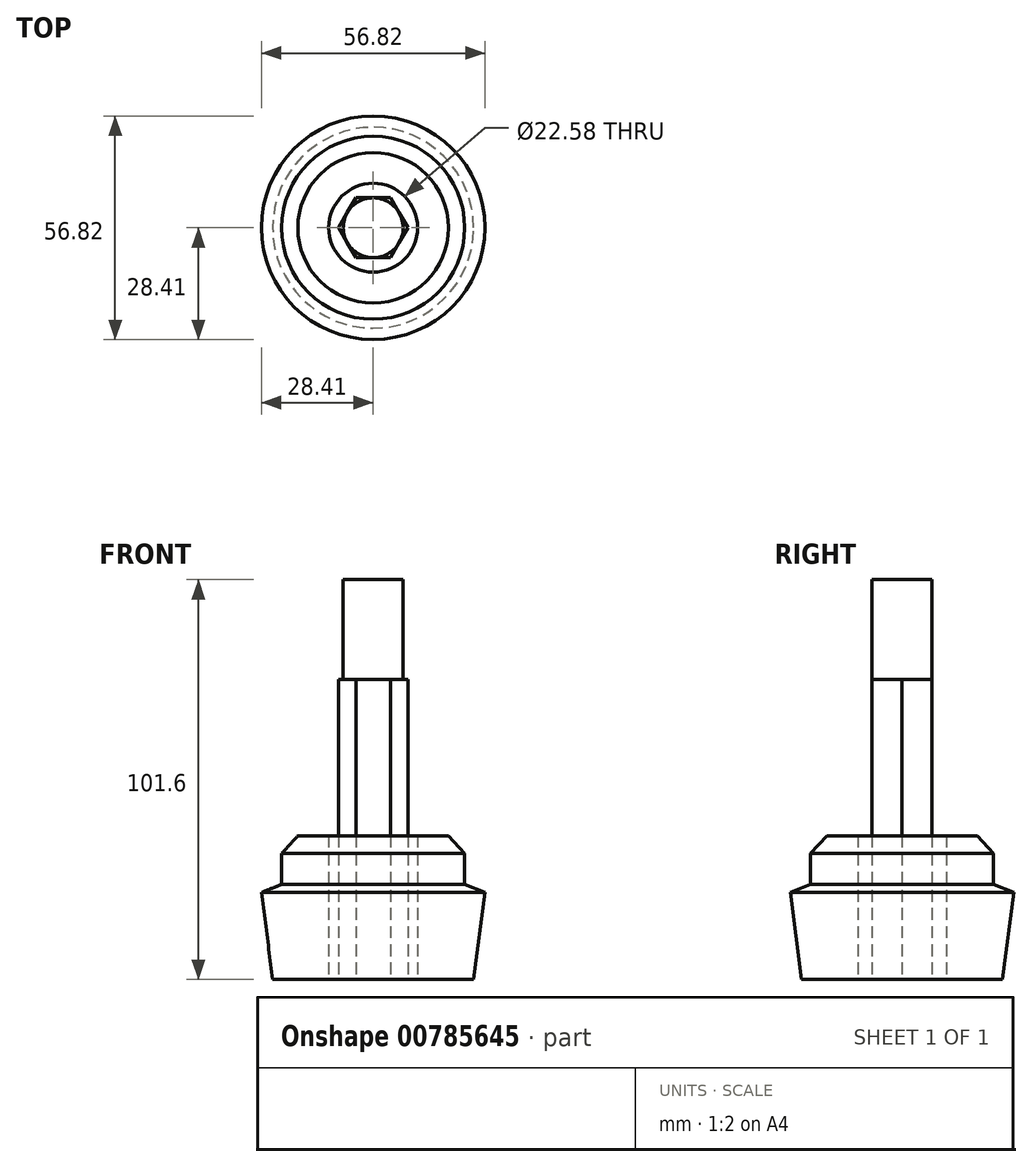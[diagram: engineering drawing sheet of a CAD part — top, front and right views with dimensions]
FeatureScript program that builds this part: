
annotation { "Feature Type Name" : "Feature", "Feature Type Description" : "" }
export const myFeature = defineFeature(function(context is Context, id is Id, definition is map)
    precondition{}
    {
        {
            var Q0;
            Q0=qCreatedBy(makeId("Front.planeOp"),FACE);
            var sketch = newSketch(context, id + "F0", { "sketchPlane" : qUnion([Q0])});
            skLineSegment(sketch, "E0", {"start": v(0, 0) * mm, "end": v(0, 43.15) * mm, "construction": true});
            skLineSegment(sketch, "E1", {"start": v(11.3, 0) * mm, "end": v(11.3, 36.55) * mm});
            skLineSegment(sketch, "E2", {"start": v(11.3, 36.55) * mm, "end": v(19.13, 36.55) * mm});
            skLineSegment(sketch, "E3", {"start": v(19.13, 36.55) * mm, "end": v(23.25, 32.01) * mm});
            skLineSegment(sketch, "E4", {"start": v(23.25, 32.01) * mm, "end": v(23.25, 24.18) * mm});
            skLineSegment(sketch, "E5", {"start": v(23.25, 24.18) * mm, "end": v(28.4, 22.12) * mm});
            skLineSegment(sketch, "E6", {"start": v(28.4, 22.12) * mm, "end": v(25.52, 0) * mm});
            skLineSegment(sketch, "E7", {"start": v(25.52, 0) * mm, "end": v(11.3, 0) * mm});
            skSolve(sketch);
        }
        {
            var Q0;
            Q0=makeQuery(id+"F0.imprint","IMPRINT",FACE,{"disambiguationData":[TD([[makeQuery(id+"F0.imprint","IMPRINT",EDGE,{"derivedFrom":sQuery(id+"F0.wireOp",EDGE,"E1")}),-1.0]])]});
            var Q1;
            Q1=sQuery(id+"F0.wireOp",EDGE,"E0");
            revolve(context, id + "F1", {"surfaceOperationType" : NewSurfaceOperationType.NEW, "entities" : qUnion([Q0]), "axis" : qUnion([Q1]), "revolveType" : RevolveType.FULL});
        }
        {
            var Q0;
            Q0=qCreatedBy(makeId("Top.planeOp"),FACE);
            var sketch = newSketch(context, id + "F2", { "sketchPlane" : qUnion([Q0])});
            skCircle(sketch, "E8.cCircle", {"center": v(0, 0) * mm, "radius": 7.6 * mm});
            skLineSegment(sketch, "E8.0", {"start": v(-4.4, 7.6) * mm, "end": v(4.4, 7.6) * mm});
            skLineSegment(sketch, "E8.1", {"start": v(4.4, 7.6) * mm, "end": v(8.79, 0) * mm});
            skLineSegment(sketch, "E8.2", {"start": v(8.79, 0) * mm, "end": v(4.4, -7.6) * mm});
            skLineSegment(sketch, "E8.3", {"start": v(4.4, -7.6) * mm, "end": v(-4.4, -7.6) * mm});
            skLineSegment(sketch, "E8.4", {"start": v(-4.4, -7.6) * mm, "end": v(-8.79, 0) * mm});
            skLineSegment(sketch, "E8.5", {"start": v(-8.79, 0) * mm, "end": v(-4.4, 7.6) * mm});
            skPoint(sketch, "E8.0.midPoint", {"position": v(0, 7.6) * mm});
            skSolve(sketch);
        }
        {
            var Q0;
            {var subQ0=sQuery(id+"F2.wireOp",EDGE,"E8.cCircle");var subQ4=makeQuery(id+"F2.imprint","INTERSECT",VERTEX,{"derivedFrom":[subQ0,sQuery(id+"F2.wireOp",EDGE,"E8.0")]});Q0=makeQuery(id+"F2.imprint","IMPRINT",FACE,{"disambiguationData":[TD([[makeQuery(id+"F2.imprint","IMPRINT",EDGE,{"disambiguationData":[TD([[subQ4,1.0]])],"derivedFrom":subQ0}),1.0]])]});}
            extrude(context, id + "F3", {"entities" : qUnion([Q0]), "depth" : 101.6 * mm, "offsetDistance" : 25.4 * mm});
        }
        {
            var Q0;
            {var subQ0=sQuery(id+"F2.wireOp",EDGE,"E8.cCircle");var subQ4=makeQuery(id+"F2.imprint","INTERSECT",VERTEX,{"derivedFrom":[subQ0,sQuery(id+"F2.wireOp",EDGE,"E8.0")]});Q0=makeQuery(id+"F2.imprint","IMPRINT",FACE,{"disambiguationData":[TD([[makeQuery(id+"F2.imprint","IMPRINT",EDGE,{"disambiguationData":[TD([[subQ4,1.0]])],"derivedFrom":subQ0}),1.0]])]});}
            var Q1;
            {var subQ0=sQuery(id+"F2.wireOp",EDGE,"E8.0");var subQ1=sQuery(id+"F2.wireOp",EDGE,"E8.cCircle");var subQ2=makeQuery(id+"F2.imprint","INTERSECT",VERTEX,{"derivedFrom":[subQ1,subQ0]});Q1=makeQuery(id+"F2.imprint","IMPRINT",FACE,{"disambiguationData":[TD([[makeQuery(id+"F2.imprint","IMPRINT",EDGE,{"disambiguationData":[TD([[subQ2,-1.0]])],"derivedFrom":subQ1}),-1.0]])]});}
            var Q2;
            {var subQ0=sQuery(id+"F2.wireOp",EDGE,"E8.0");var subQ1=sQuery(id+"F2.wireOp",EDGE,"E8.cCircle");var subQ2=makeQuery(id+"F2.imprint","INTERSECT",VERTEX,{"derivedFrom":[subQ1,subQ0]});Q2=makeQuery(id+"F2.imprint","IMPRINT",FACE,{"disambiguationData":[TD([[makeQuery(id+"F2.imprint","IMPRINT",EDGE,{"disambiguationData":[TD([[subQ2,1.0]])],"derivedFrom":subQ1}),-1.0]])]});}
            var Q3;
            {var subQ0=sQuery(id+"F2.wireOp",EDGE,"E8.1");var subQ1=sQuery(id+"F2.wireOp",EDGE,"E8.cCircle");var subQ2=makeQuery(id+"F2.imprint","INTERSECT",VERTEX,{"derivedFrom":[subQ1,subQ0]});Q3=makeQuery(id+"F2.imprint","IMPRINT",FACE,{"disambiguationData":[TD([[makeQuery(id+"F2.imprint","IMPRINT",EDGE,{"disambiguationData":[TD([[subQ2,1.0]])],"derivedFrom":subQ1}),-1.0]])]});}
            var Q4;
            {var subQ0=sQuery(id+"F2.wireOp",EDGE,"E8.3");var subQ1=sQuery(id+"F2.wireOp",EDGE,"E8.cCircle");var subQ2=makeQuery(id+"F2.imprint","INTERSECT",VERTEX,{"derivedFrom":[subQ1,subQ0]});Q4=makeQuery(id+"F2.imprint","IMPRINT",FACE,{"disambiguationData":[TD([[makeQuery(id+"F2.imprint","IMPRINT",EDGE,{"disambiguationData":[TD([[subQ2,-1.0]])],"derivedFrom":subQ1}),-1.0]])]});}
            var Q5;
            {var subQ0=sQuery(id+"F2.wireOp",EDGE,"E8.4");var subQ1=sQuery(id+"F2.wireOp",EDGE,"E8.cCircle");var subQ2=makeQuery(id+"F2.imprint","INTERSECT",VERTEX,{"derivedFrom":[subQ1,subQ0]});Q5=makeQuery(id+"F2.imprint","IMPRINT",FACE,{"disambiguationData":[TD([[makeQuery(id+"F2.imprint","IMPRINT",EDGE,{"disambiguationData":[TD([[subQ2,-1.0]])],"derivedFrom":subQ1}),-1.0]])]});}
            var Q6;
            {var subQ0=sQuery(id+"F2.wireOp",EDGE,"E8.5");var subQ1=sQuery(id+"F2.wireOp",EDGE,"E8.cCircle");var subQ2=makeQuery(id+"F2.imprint","INTERSECT",VERTEX,{"derivedFrom":[subQ1,subQ0]});Q6=makeQuery(id+"F2.imprint","IMPRINT",FACE,{"disambiguationData":[TD([[makeQuery(id+"F2.imprint","IMPRINT",EDGE,{"disambiguationData":[TD([[subQ2,-1.0]])],"derivedFrom":subQ1}),-1.0]])]});}
            extrude(context, id + "F4", {"entities" : qUnion([Q0, Q1, Q2, Q3, Q4, Q5, Q6]), "operationType" : NewBodyOperationType.ADD, "depth" : 76.2 * mm, "offsetDistance" : 25.4 * mm});
        }
    });
